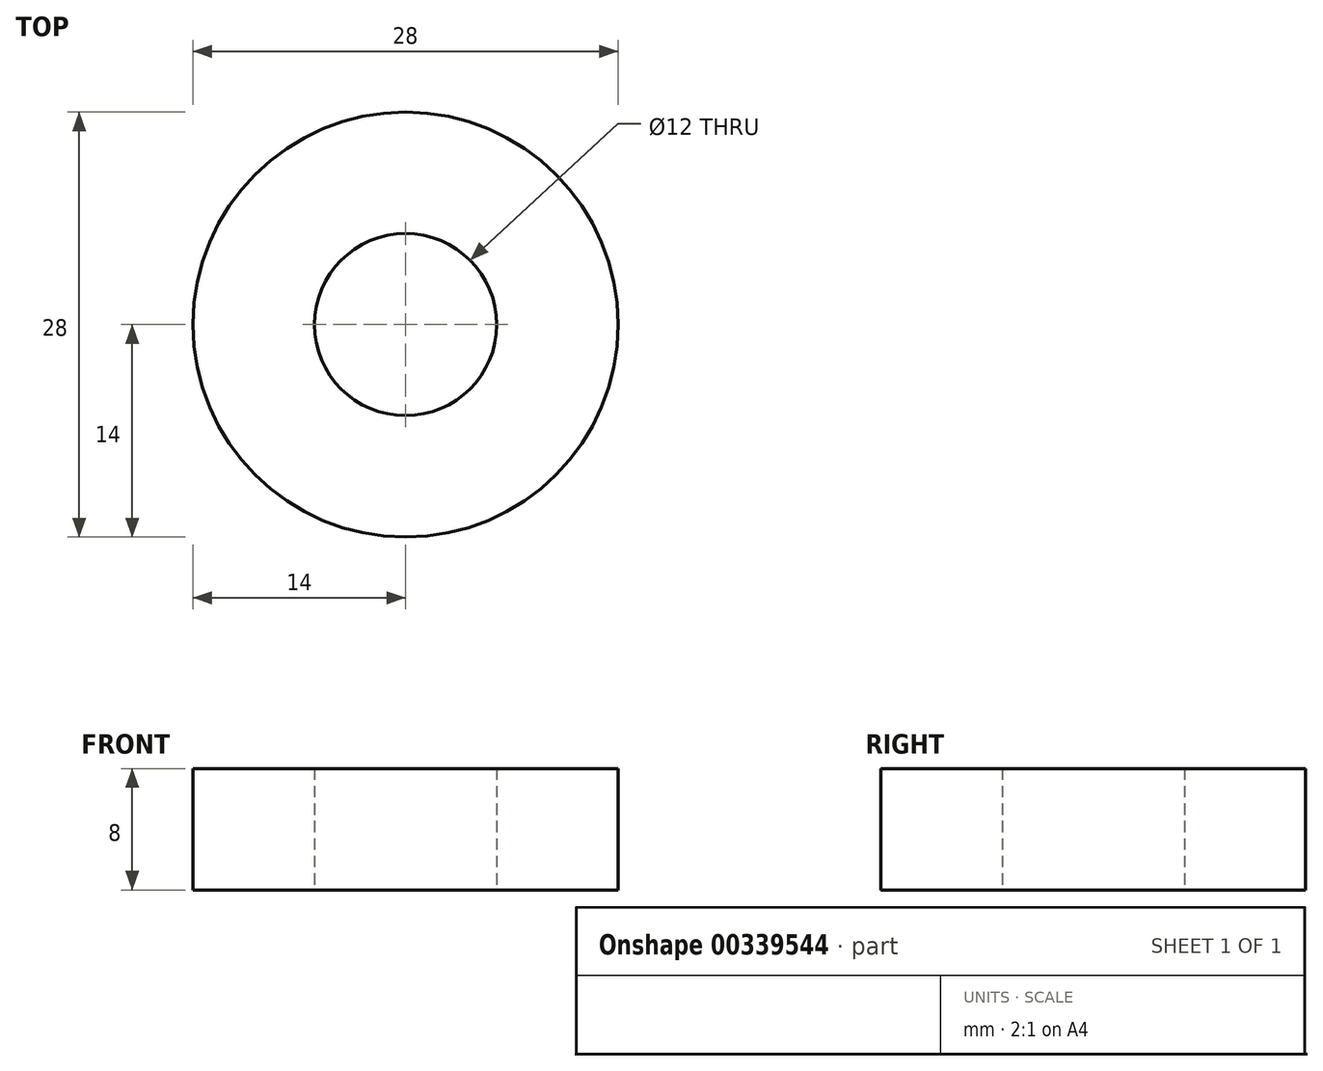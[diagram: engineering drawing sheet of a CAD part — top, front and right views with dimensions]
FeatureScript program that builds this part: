
annotation { "Feature Type Name" : "Feature", "Feature Type Description" : "" }
export const myFeature = defineFeature(function(context is Context, id is Id, definition is map)
    precondition{}
    {
        {
            var Q0;
            Q0=qCreatedBy(makeId("Top.planeOp"),FACE);
            var sketch = newSketch(context, id + "F0", { "sketchPlane" : qUnion([Q0])});
            skCircle(sketch, "E0", {"center": v(0, 0) * mm, "radius": 6 * mm});
            skCircle(sketch, "E1", {"center": v(0, 0) * mm, "radius": 14 * mm});
            skSolve(sketch);
        }
        {
            var Q0;
            Q0=makeQuery(id+"F0.imprint","IMPRINT",FACE,{"disambiguationData":[TD([[makeQuery(id+"F0.imprint","IMPRINT",EDGE,{"derivedFrom":sQuery(id+"F0.wireOp",EDGE,"E0")}),-1.0]])]});
            extrude(context, id + "F1", {"entities" : qUnion([Q0]), "depth" : 8 * mm});
        }
    });
